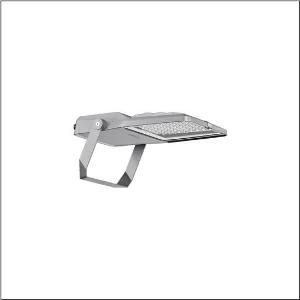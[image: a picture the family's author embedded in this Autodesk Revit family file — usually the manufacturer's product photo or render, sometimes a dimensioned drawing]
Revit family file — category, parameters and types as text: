
# Revit family: floodlight_fl_21_iq_mini___rs12_5xa7771b2b1a_fd88
name_source: partatom
category: Lighting Fixtures
units: mm (PartAtom-declared; Revit-internal decimal feet)

## family parameters
Cut with Voids When Loaded = No
Host = Face
Light Source = No
Part Type = Normal
Room Calculation Point = No
Round Connector Dimension = Use Diameter
Shared = No

## types (1)
- --- (1 x LED, 6300 lm, 45.5 W, 3000K)
    Apparent Load = 46 VA
    CIE Flux Codes = 79 92 99 100 100
    Color Rendering = 70
    Color Temperature = 3000K
    Default Elevation = 1800 mm
    Description = Floodlight FL 21 iQ mini, floodlight, primary light control with lens, of PMMA, primary optical cover: protective disc, of toughened safety glass, transparent, light distribution: RS12, light emission: direct distribution, installation type: surface-mounted, lamps: LED, High Power LED, rated values: 6.300lm | 45,5W | 138,5lm/W (begin service life); end service life: 6.300lm | 48W; at 50% lumin. flux: 3.150lm | 21,5W | 146,5lm/W, colour temperature: 3000K, colour rendering: CRI > 70, light colour: 730, light setting 1 begin service life: 100% | 6.300lm | 45,5W | 138,5lm/W | 3.000K, light setting 1 end service life: 48W, further light settings possible, control: Auto-Match, Temp-Guard, Lumen-Switch, Night-Set, Smart-Wire, Light-Fading, Desk-Remote (wireless, voltage-free reading and setting of iQ features in the workshop via application-optimized NFC function/RFID function), optimised constant luminous flux control (CLO 2.0), pre-setting: linear dimming characteristic, with terminal, 6-pole, mains connection: 220..240V, AC, 50/60Hz, luminaire housing, of diecast aluminium, powder-coated, SITECO metallic grey (DB 702S), corrosivity category C5 mid according to DIN EN ISO 12944suitable for swimming poolschlorine-resistant, sealing non-destructively replaceable, mounting bracket, of steel, galvanised, powder-coated, SITECO metallic grey (DB 702S), protection rating (complete): IP66, insulation class (complete): insulation class II (safety insulation), certification: CE, ENEC, VDE, protection symbol: D, impact resistance: IK08, permissible operating ambient temperature: -40..+40°C, permissible operating ambient temperature for outdoor applications: -40..+50°C, standard: DIN EN 12944, LABS conformity tested according to VDMA 24364:2018-05, packaging unit: 1 piece

Light Distribution: RS12
    Height = 70 mm
    Lamp = 1 x LED
    Lamp Light Flux = 6300 lm
    Lamp Power = 45.5 W
    Lamp count = 1
    Length = 485 mm
    Luminous efficacy = 138 lm/W
    Manufacturer = Siteco
    ModVariant = No
    Model = 5XA7771B2B1A
    Mounting Place = Wall
    Mounting Type = Surface mounted
    Number of Poles = 1
    OnlyDefault = Yes
    Power Factor = 1
    Product Name = Floodlight FL 21 iQ mini | RS12
    Product group = floodlight | wall mounted
    ProductGroupID = 2002
    Protection Class = Protection class II
    Protection Degree = IP 66
    RLX_Detail_Level = 1
    RLX_Emergency_Light_Flux = 0 lm
    RLX_Emergency_Type = 0
    RLX_Emergency_Type_DB = No
    RlxData = <blob elided: 90993 chars, md5=b6d9b67c>
    Socket = socket
    Standby Power = 0 W
    System Light Flux = 6300 lm
    System Power = 46 W
    Type Comments = factory setting: luminous flux: 100 % | dim-lin: 254 | 463 mA
    Type Image = l_1006845.jpg
    URL = http://relux.com
    VarID = @adj_169029
    Voltage = 0 V
    Weight = 0.00 kg
    Width = 337 mm

## geometry (parser evidence)
native form markers: Blend x4, Sweep x13
no freeform markers — native parametric forms only
